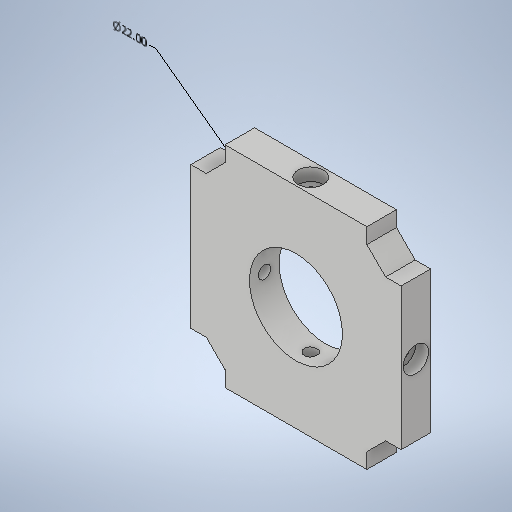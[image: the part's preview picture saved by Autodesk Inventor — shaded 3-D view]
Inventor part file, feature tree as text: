
AUTODESK INVENTOR PART (.ipt)
format: ipt  version: 2025 (Build 290162000, 162)  size: 300,032 bytes
history: native  units: mm
features: sketch x6, hole x5, extrude x1, other x1
ambient origin geometry x8: Origin, YZ Plane, XZ Plane, XY Plane, X Axis, Y Axis, Z Axis, Center Point
bodies: 实体1 (feature_tree)
feature tree (13):
  extrude  "拉伸1"  Depth=3.0mm
  hole  "孔1"  [1 undecoded]
  hole  "孔2"  [1 undecoded]
  hole  "孔3"  [1 undecoded]
  hole  "孔4"  [1 undecoded]
  hole  "孔5"  [1 undecoded]
  sketch  "草图1"  dims[d18=7.0mm d19=0.0mm]
  sketch  "草图2"  dims[d20=2.97mm d21=6.0mm d22=6.0mm d23=3.0mm d24=90.0deg d25=8.0mm d26=20.594885mm]
  sketch  "草图3"  dims[d27=2.97mm d28=6.0mm d29=6.0mm d30=3.0mm d31=90.0deg d32=8.0mm d33=20.594885mm]
  sketch  "草图4"  dims[d34=2.97mm d35=6.0mm d36=6.0mm d37=3.0mm d38=90.0deg d39=8.0mm d40=20.594885mm]
  sketch  "草图5"  dims[d41=2.97mm d42=6.0mm d43=6.0mm d44=3.0mm d45=90.0deg d46=8.0mm d47=20.594885mm]
  sketch  "草图6"  dims[d48=22.0mm d49=6.0mm d50=6.0mm d51=3.0mm d52=90.0deg d53=0.5mm d54=20.594885mm d55=6.326251mm d56=22.0mm]
  other  "直径尺寸 1"
note: 5 required parameter values undecoded (feature->parameter linkage not recoverable at this tier; creation-order binding heuristic only, values carry confidence <= 0.55)
